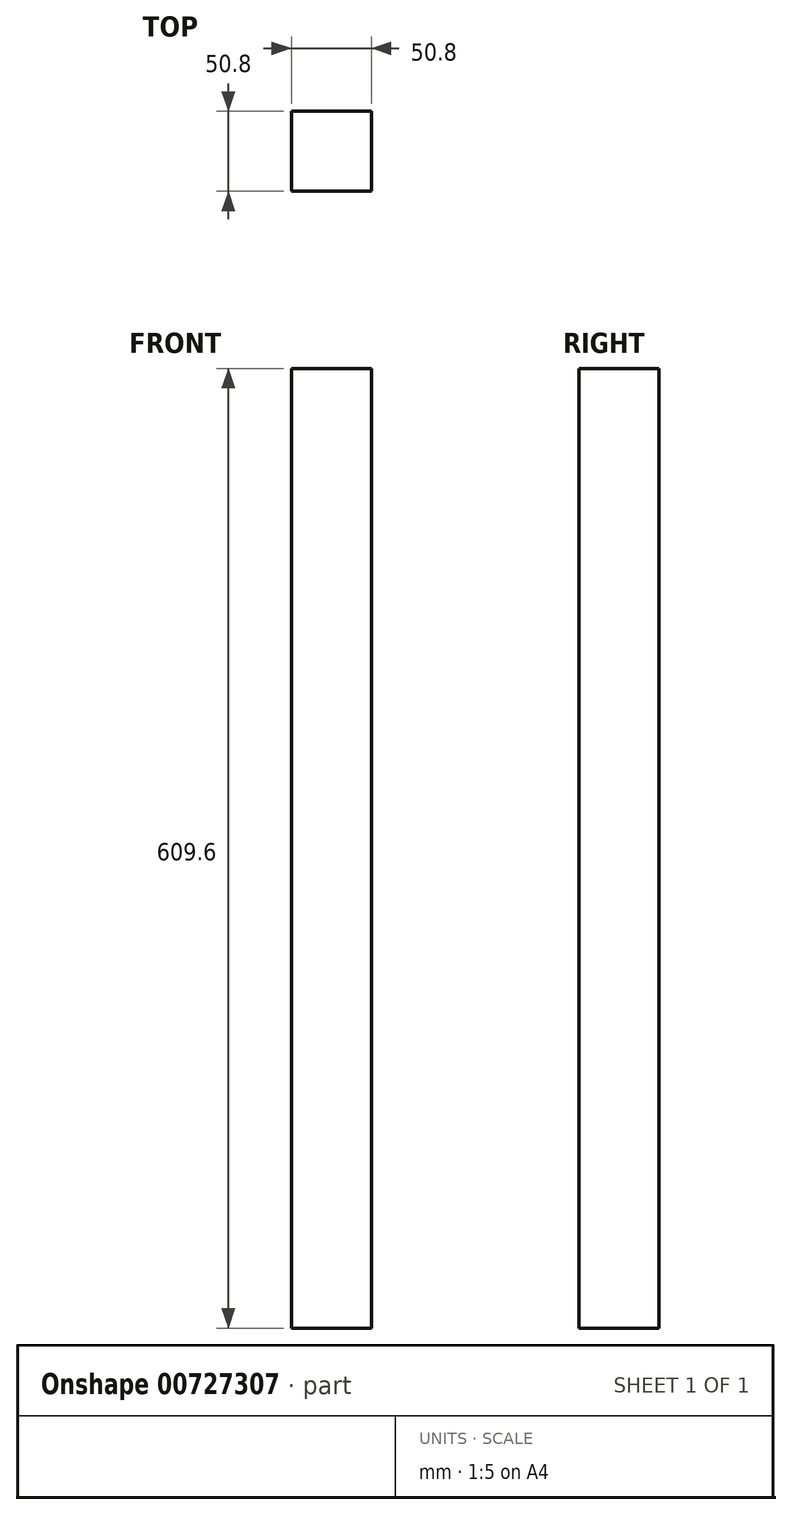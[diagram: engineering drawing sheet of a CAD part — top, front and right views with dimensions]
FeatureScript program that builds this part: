
annotation { "Feature Type Name" : "Feature", "Feature Type Description" : "" }
export const myFeature = defineFeature(function(context is Context, id is Id, definition is map)
    precondition{}
    {
        {
            var Q0;
            Q0=qCreatedBy(makeId("Top.planeOp"),FACE);
            var sketch = newSketch(context, id + "F0", { "sketchPlane" : qUnion([Q0])});
            skLineSegment(sketch, "E0.bottom", {"start": v(-126.4, -50.8) * mm, "end": v(-75.6, -50.8) * mm});
            skLineSegment(sketch, "E0.top", {"start": v(-126.4, 0) * mm, "end": v(-75.6, 0) * mm});
            skLineSegment(sketch, "E0.left", {"start": v(-126.4, -50.8) * mm, "end": v(-126.4, 0) * mm});
            skLineSegment(sketch, "E0.right", {"start": v(-75.6, -50.8) * mm, "end": v(-75.6, 0) * mm});
            skSolve(sketch);
        }
        {
            var Q0;
            Q0 = qSketchRegion(id + "F0", true);
            extrude(context, id + "F1", {"entities" : qUnion([Q0]), "depth" : 609.6 * mm, "offsetDistance" : 25.4 * mm});
        }
    });
